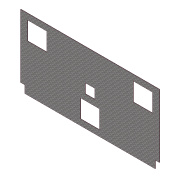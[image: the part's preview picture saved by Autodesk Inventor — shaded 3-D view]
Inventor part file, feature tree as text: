
AUTODESK INVENTOR PART (.ipt)
format: ipt  version: 2012 (Build 160160000, 160)  size: 135,680 bytes
history: native  units: in
note: dims shown in document units (in); Inventor stores cm internally (conversion verified against a paired STEP export)
features: extrude x2, sketch x2, plane x1
ambient origin geometry x8: Origin, YZ Plane, XZ Plane, XY Plane, X Axis, Y Axis, Z Axis, Center Point
bodies: Solid1 (feature_tree)
feature tree (5):
  extrude  "Extrusion1"  Depth=36.75in
  plane  "Work Plane1"
  extrude  "Extrusion2"  Depth=0.05in
  sketch  "Sketch1"  dims[d0=72.0in d1=36.75in]
  sketch  "Sketch5"  dims[d2=0.1875in d3=0.0in d38=0.05in d55=3.5625in d56=24.25in d57=3.0in d58=10.0in d59=3.5625in d60=31.0in d61=72.0in d62=1.0in d63=0.0in d64=9.5in d65=10.0in d66=9.5in d67=3.875in d68=2.125in d69=5.0in d70=2.5in d71=3.0in]
